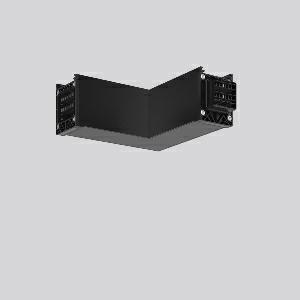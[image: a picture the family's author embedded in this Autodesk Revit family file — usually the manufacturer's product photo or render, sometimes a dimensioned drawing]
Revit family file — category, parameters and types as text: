
# Revit family: linedo_l-verbindung_982773_003_7_fd1a
name_source: partatom
category: Lighting Fixtures
units: mm (PartAtom-declared; Revit-internal decimal feet)

## family parameters
Cut with Voids When Loaded = No
Host = Face
Light Source = No
Part Type = Normal
Room Calculation Point = No
Round Connector Dimension = Use Diameter
Shared = No

## types (1)
- LINEDO L-Verbindung
    Apparent Load = 0 VA
    Default Elevation = 1800 mm
    Description = Series: LINEDO
L-connector, 7-pole, connection socket / plug. Housing: extruded aluminium profile, powder-coated. Cover made of plastic, surface like housing. LINEDO plug system, plastic, black. Easy connection for rigid or flexible wires. 2 membrane cable entries (M25). Suitable for power supply in 7-pole version. Ready prewired. Colour-coded individual cables enable easy electromechanical separation.
Colour: jet black (RAL 9005)
Length: 185 mm
Width: 204 mm
Height: 76 mm
Weight: 640 g
    Height = 76 mm
    Lamp = 0 x
    Length = 185 mm
    Luminous efficacy = 0 lm/W
    Manufacturer = RZB
    ModVariant = No
    Model = 982773.003.7
    Mounting Place = Ceiling
    Mounting Type = Surface mounted
    Number of Poles = 1
    OnlyDefault = Yes
    Power Factor = 1
    Product Name = LINEDO L-Verbindung
    Product group = Surface mounted continuous line luminaire system
    ProductGroupID = 310
    Protection Class = Protection class I
    Protection Degree = Degree of protection
    RLX_Detail_Level = 1
    RLX_Emergency_Light_Flux = 0 lm
    RLX_Emergency_Type = 0
    RLX_Emergency_Type_DB = No
    RlxData = <blob elided: 19093 chars, md5=19e46b88>
    Standby Power = 0 W
    System Light Flux = 0 lm
    System Power = 0 W
    Type Comments = Product without accessories
    Type Image = 982773.003.3.jpg
    URL = http://relux.com
    VarID = ---
    Voltage = 0 V
    Weight = 0.00 kg
    Width = 204 mm

## geometry (parser evidence)
native form markers: Blend x4, Sweep x12
no freeform markers — native parametric forms only
